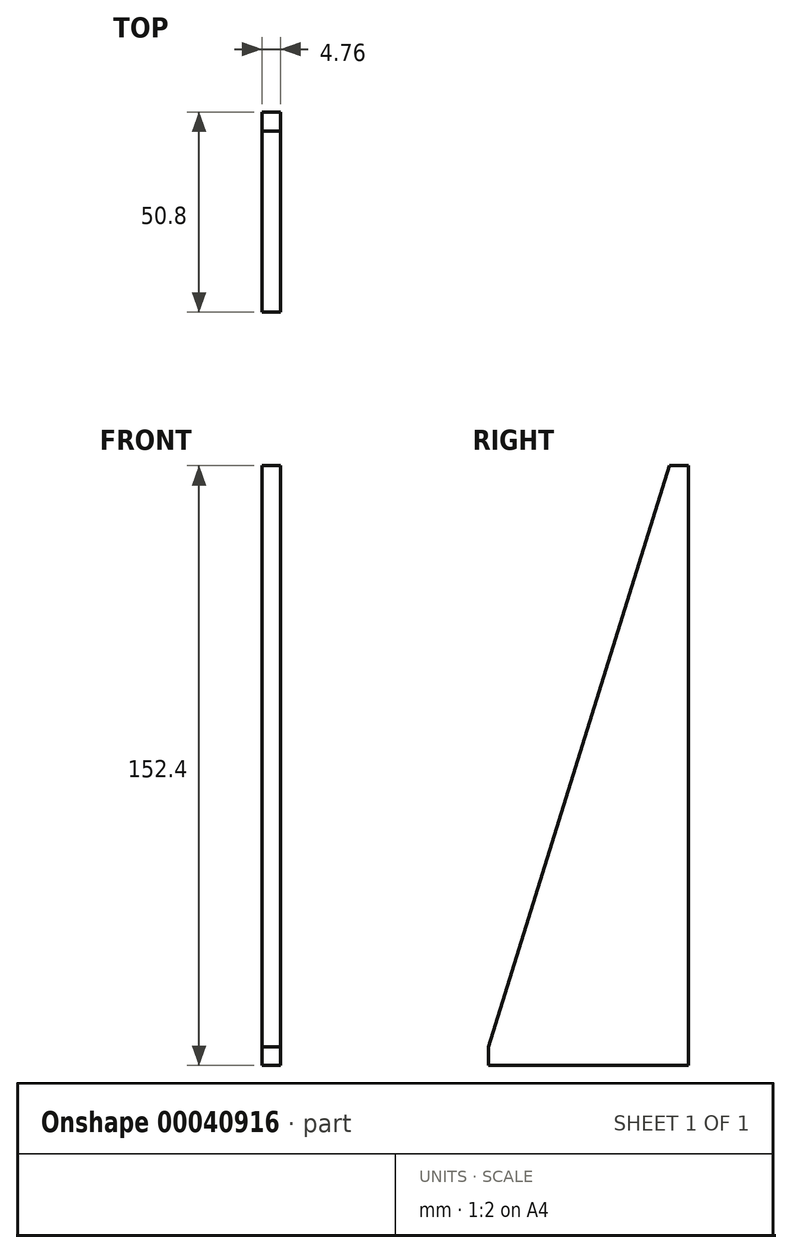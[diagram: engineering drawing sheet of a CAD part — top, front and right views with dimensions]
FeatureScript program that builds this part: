
annotation { "Feature Type Name" : "Feature", "Feature Type Description" : "" }
export const myFeature = defineFeature(function(context is Context, id is Id, definition is map)
    precondition{}
    {
        {
            var Q0;
            Q0=qCreatedBy(makeId("Right.planeOp"),FACE);
            var sketch = newSketch(context, id + "F0", { "sketchPlane" : qUnion([Q0])});
            skLineSegment(sketch, "E0", {"start": v(0, 0) * mm, "end": v(0, 152.4) * mm});
            skLineSegment(sketch, "E1", {"start": v(-50.8, 0) * mm, "end": v(0, 0) * mm});
            skLineSegment(sketch, "E2", {"start": v(-50.8, 0) * mm, "end": v(-50.8, 4.76) * mm});
            skLineSegment(sketch, "E3", {"start": v(0, 152.4) * mm, "end": v(-4.76, 152.4) * mm});
            skLineSegment(sketch, "E4", {"start": v(-4.76, 152.4) * mm, "end": v(-50.8, 4.76) * mm});
            skSolve(sketch);
        }
        {
            var Q0;
            Q0 = qSketchRegion(id + "F0", true);
            extrude(context, id + "F1", {"entities" : qUnion([Q0]), "depth" : 4.76 * mm});
        }
    });
